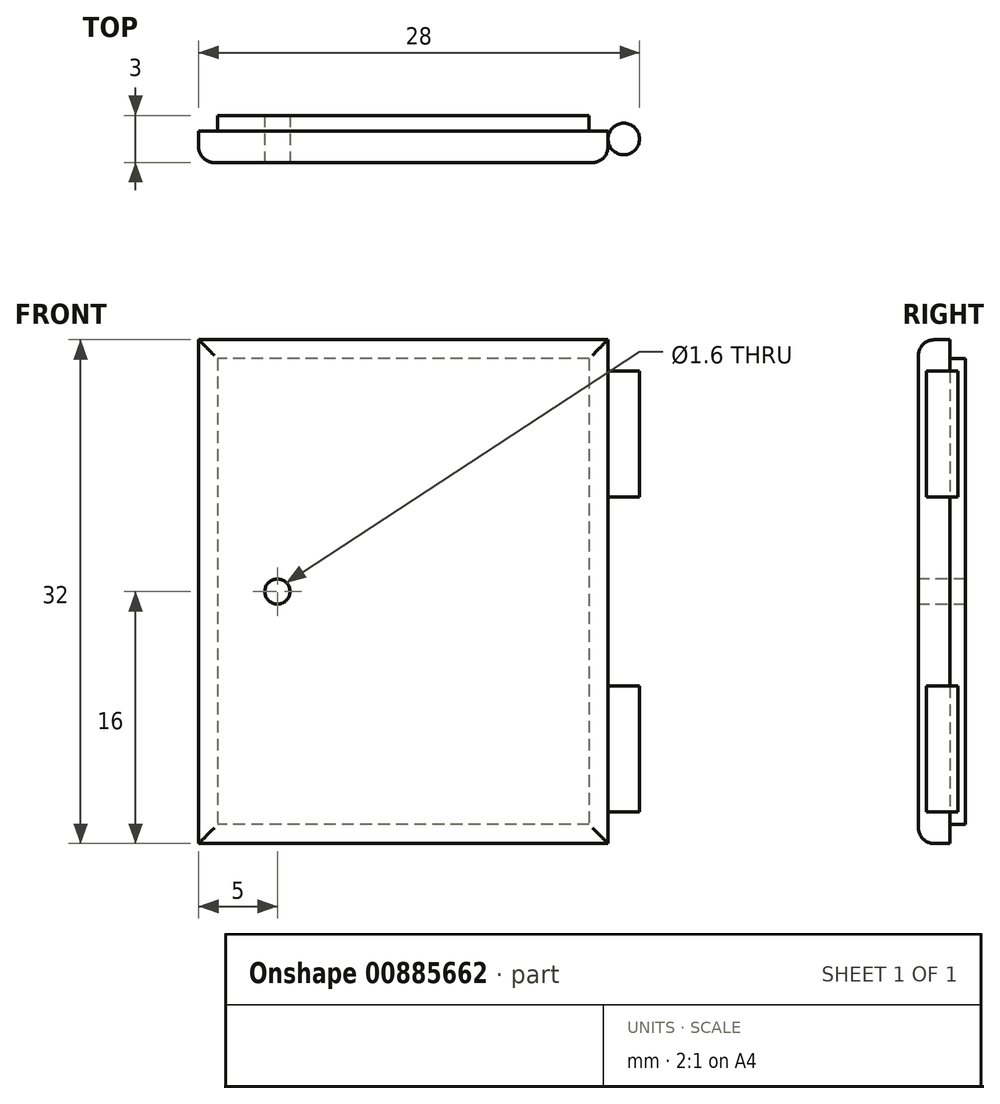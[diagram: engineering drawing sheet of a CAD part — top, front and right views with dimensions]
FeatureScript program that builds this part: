
annotation { "Feature Type Name" : "Feature", "Feature Type Description" : "" }
export const myFeature = defineFeature(function(context is Context, id is Id, definition is map)
    precondition{}
    {
        {
            var Q0;
            Q0=qCreatedBy(makeId("Front.planeOp"),FACE);
            var sketch = newSketch(context, id + "F0", { "sketchPlane" : qUnion([Q0])});
            skLineSegment(sketch, "E0.bottom", {"start": v(13, 16) * mm, "end": v(-13, 16) * mm});
            skLineSegment(sketch, "E0.top", {"start": v(13, -16) * mm, "end": v(-13, -16) * mm});
            skLineSegment(sketch, "E0.left", {"start": v(13, 16) * mm, "end": v(13, -16) * mm});
            skLineSegment(sketch, "E0.right", {"start": v(-13, 16) * mm, "end": v(-13, -16) * mm});
            skPoint(sketch, "E0.middle", {"position": v(0, 0) * mm});
            skLineSegment(sketch, "E1.0", {"start": v(-11.8, 14.8) * mm, "end": v(-11.8, -14.8) * mm});
            skLineSegment(sketch, "E1.1", {"start": v(11.8, 14.8) * mm, "end": v(-11.8, 14.8) * mm});
            skLineSegment(sketch, "E1.2", {"start": v(11.8, 14.8) * mm, "end": v(11.8, -14.8) * mm});
            skLineSegment(sketch, "E1.3", {"start": v(11.8, -14.8) * mm, "end": v(-11.8, -14.8) * mm});
            skSolve(sketch);
        }
        {
            var Q0;
            Q0=makeQuery(id+"F0.imprint","IMPRINT",FACE,{"disambiguationData":[TD([[makeQuery(id+"F0.imprint","IMPRINT",EDGE,{"derivedFrom":sQuery(id+"F0.wireOp",EDGE,"E1.0")}),1.0]])]});
            extrude(context, id + "F1", {"entities" : qUnion([Q0]), "oppositeDirection" : true, "depth" : 1 * mm, "offsetDistance" : 25 * mm});
        }
        {
            var Q0;
            Q0=makeQuery(id+"F0.imprint","IMPRINT",FACE,{"disambiguationData":[TD([[makeQuery(id+"F0.imprint","IMPRINT",EDGE,{"derivedFrom":sQuery(id+"F0.wireOp",EDGE,"E0.bottom")}),1.0]])]});
            var Q1;
            Q1=makeQuery(id+"F0.imprint","IMPRINT",FACE,{"disambiguationData":[TD([[makeQuery(id+"F0.imprint","IMPRINT",EDGE,{"derivedFrom":sQuery(id+"F0.wireOp",EDGE,"E1.0")}),1.0]])]});
            extrude(context, id + "F2", {"entities" : qUnion([Q0, Q1]), "operationType" : NewBodyOperationType.ADD, "depth" : 2 * mm, "offsetDistance" : 25 * mm});
        }
        {
            var Q0;
            Q0=makeQuery(id+"F2.opExtrude","CAP_FACE",FACE,{"disambiguationData":[OSD([sQuery(id+"F0.wireOp",EDGE,"E0.bottom"),sQuery(id+"F0.wireOp",EDGE,"E0.top"),sQuery(id+"F0.wireOp",EDGE,"E0.left"),sQuery(id+"F0.wireOp",EDGE,"E0.right")])],"isStart":false});
            fillet(context, id + "F3", {"entities" : qUnion([Q0]), "radius" : 1 * mm, "tangentPropagation" : true, "allowEdgeOverflow" : false});
        }
        {
            var Q0;
            Q0=makeQuery(id+"F2.opExtrude","CAP_FACE",FACE,{"disambiguationData":[OSD([sQuery(id+"F0.wireOp",EDGE,"E0.bottom"),sQuery(id+"F0.wireOp",EDGE,"E0.top"),sQuery(id+"F0.wireOp",EDGE,"E0.left"),sQuery(id+"F0.wireOp",EDGE,"E0.right")])],"isStart":false});
            var sketch = newSketch(context, id + "F4", { "sketchPlane" : qUnion([Q0])});
            skLineSegment(sketch, "E2", {"start": v(-12, 0) * mm, "end": v(-8, 0) * mm, "construction": true});
            skCircle(sketch, "E3", {"center": v(-8, 0) * mm, "radius": 0.8 * mm});
            skSolve(sketch);
        }
        {
            var Q0;
            Q0=makeQuery(id+"F4.imprint","IMPRINT",FACE,{"disambiguationData":[TD([[makeQuery(id+"F4.imprint","IMPRINT",EDGE,{"derivedFrom":sQuery(id+"F4.wireOp",EDGE,"E3")}),1.0]])]});
            extrude(context, id + "F5", {"entities" : qUnion([Q0]), "operationType" : NewBodyOperationType.REMOVE, "oppositeDirection" : true, "depth" : 5 * mm, "offsetDistance" : 25 * mm});
        }
        {
            var Q0;
            Q0=makeQuery(id+"F2.opExtrude","SWEPT_FACE",FACE,{"disambiguationData":[OSD([sQuery(id+"F0.wireOp",EDGE,"E0.bottom")])]});
            var sketch = newSketch(context, id + "F6", { "sketchPlane" : qUnion([Q0])});
            skLineSegment(sketch, "E4", {"start": v(13, -0.5) * mm, "end": v(14, -0.5) * mm, "construction": true});
            skCircle(sketch, "E5", {"center": v(14, -0.5) * mm, "radius": 1 * mm});
            skSolve(sketch);
        }
        {
            var Q0;
            Q0=makeQuery(id+"F6.imprint","IMPRINT",FACE,{"disambiguationData":[TD([[makeQuery(id+"F6.imprint","IMPRINT",EDGE,{"derivedFrom":sQuery(id+"F6.wireOp",EDGE,"E5")}),1.0]])]});
            extrude(context, id + "F7", {"entities" : qUnion([Q0]), "oppositeDirection" : true, "depth" : 10 * mm, "offsetDistance" : 25 * mm});
        }
        {
            var Q0;
            Q0=makeQuery(id+"F7.opExtrude","CAP_FACE",FACE,{"disambiguationData":[OSD([sQuery(id+"F6.wireOp",EDGE,"E5")])],"isStart":true});
            extrude(context, id + "F8", {"entities" : qUnion([Q0]), "operationType" : NewBodyOperationType.REMOVE, "oppositeDirection" : true, "depth" : 2 * mm, "offsetDistance" : 25 * mm});
        }
        {
            var Q0;
            Q0=makeQuery(id+"F7.opExtrude","SWEPT_BODY",BODY,{"disambiguationData":[OSD([sQuery(id+"F6.wireOp",EDGE,"E5")])]});
            transform(context, id + "F9", {"entities" : qUnion([Q0]), "transformType" : TransformType.TRANSLATION_3D, "dx" : 0 * mm, "dy" : 0 * mm, "dz" : -20 * mm, "makeCopy" : true});
        }
    });
